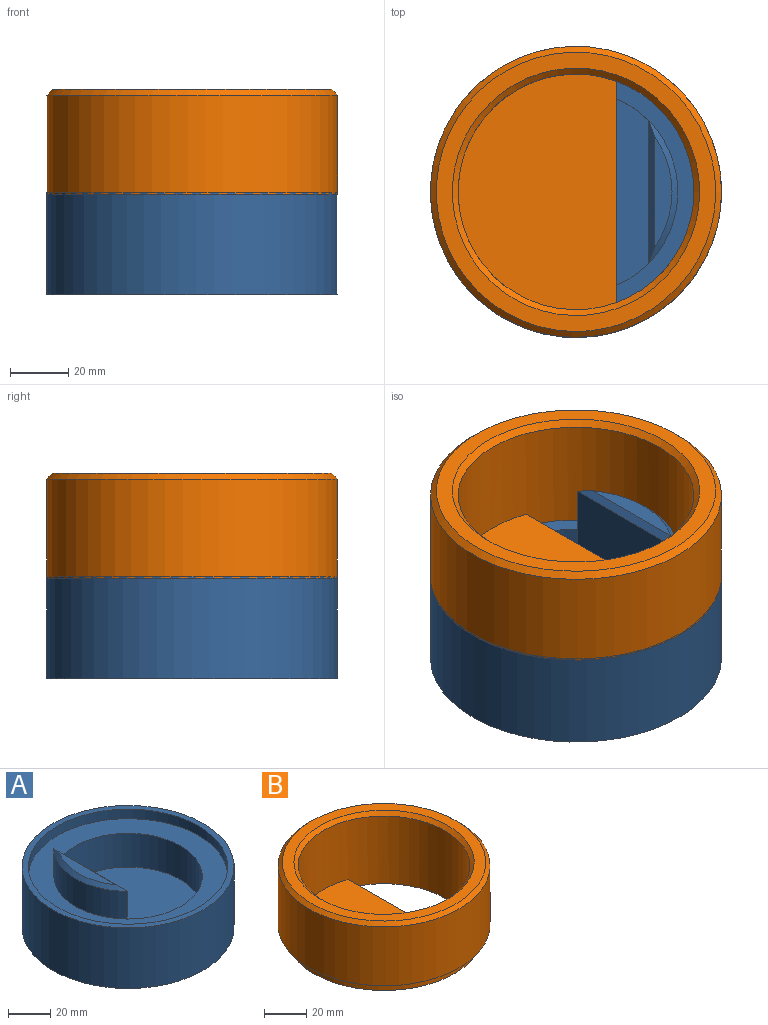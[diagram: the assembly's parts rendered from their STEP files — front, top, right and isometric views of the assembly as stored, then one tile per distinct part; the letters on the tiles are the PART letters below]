
ASSEMBLY  parts=2 mates=1
PART A: 12 faces, bbox 100x100x47.5 mm
  f0: cylinder r=35mm len=48.99mm, axis (0,0,-1), area 868.2mm2, adj f5,f6,f8
  f1: plane 37.95x6mm, normal (0,0,1), area 154.8mm2, adj f8,f9
  f2: cylinder r=50mm len=100mm, axis (0,0,-1), area 10995.6mm2, adj f3,f11
  f3: plane 100x100mm, normal (0,0,1), area 914.2mm2, adj f2,f4
  f4: cylinder r=47mm len=94mm, axis (0,0,1), area 1624.2mm2, adj f3,f5
  f5: plane 94x94mm, normal (0,0,1), area 3091.3mm2, adj f0,f4,f7
  f6: plane 48.99x35.5mm, normal (1,0,0), area 1739.1mm2, adj f0,f7,f9,f10
  f7: cylinder r=35mm len=70mm, axis (0,0,1), area 3230.1mm2, adj f5,f6,f10
  f8: cone r=35mm half-angle=45deg, axis (0,0,-1), area 134.4mm2, adj f0,f1,f9
  f9: plane 48.99x2mm, normal (0.71,0,0.71), area 123.6mm2, adj f1,f6,f8
  f10: plane 70x60mm, normal (0,0,1), area 3511.2mm2, adj f6,f7
  f11: plane 100x100mm, normal (0,0,-1), area 7854mm2, adj f2
PART B: 10 faces, bbox 100x100x41 mm
  f0: plane 81x54.5mm, normal (0,0,1), area 3687.5mm2, adj f4,f7
  f1: cylinder r=50mm len=100mm, axis (0,0,-1), area 10681.4mm2, adj f3,f9
  f2: plane 96x96mm, normal (0,0,1), area 1563.7mm2, adj f8,f9
  f3: plane 100x100mm, normal (0,0,-1), area 987.8mm2, adj f1,f6
  f4: cylinder r=40.5mm len=81mm, axis (0,0,1), area 9145.2mm2, adj f0,f5,f7,f8
  f5: plane 93.5x93.5mm, normal (0,0,-1), area 5400.6mm2, adj f4,f6,f7
  f6: cylinder r=46.75mm len=93.5mm, axis (0,0,1), area 1468.7mm2, adj f3,f5
  f7: plane 76.01x5mm, normal (1,0,0), area 380mm2, adj f0,f4,f5
  f8: cone r=40.5mm half-angle=45deg, axis (0,0,1), area 737.5mm2, adj f2,f4
  f9: cone r=48mm half-angle=45deg, axis (0,0,-1), area 870.8mm2, adj f1,f2
PLACE A rot(axis=(0,0,-1),180deg) t=(-167.33,64.87,-57.6)mm
PLACE B t=(-167.33,64.87,-33.1)mm
MATE fastened A.f2 <-> B.f6  axis (0,0,1) through (-167.33,64.87,-38.1)mm
